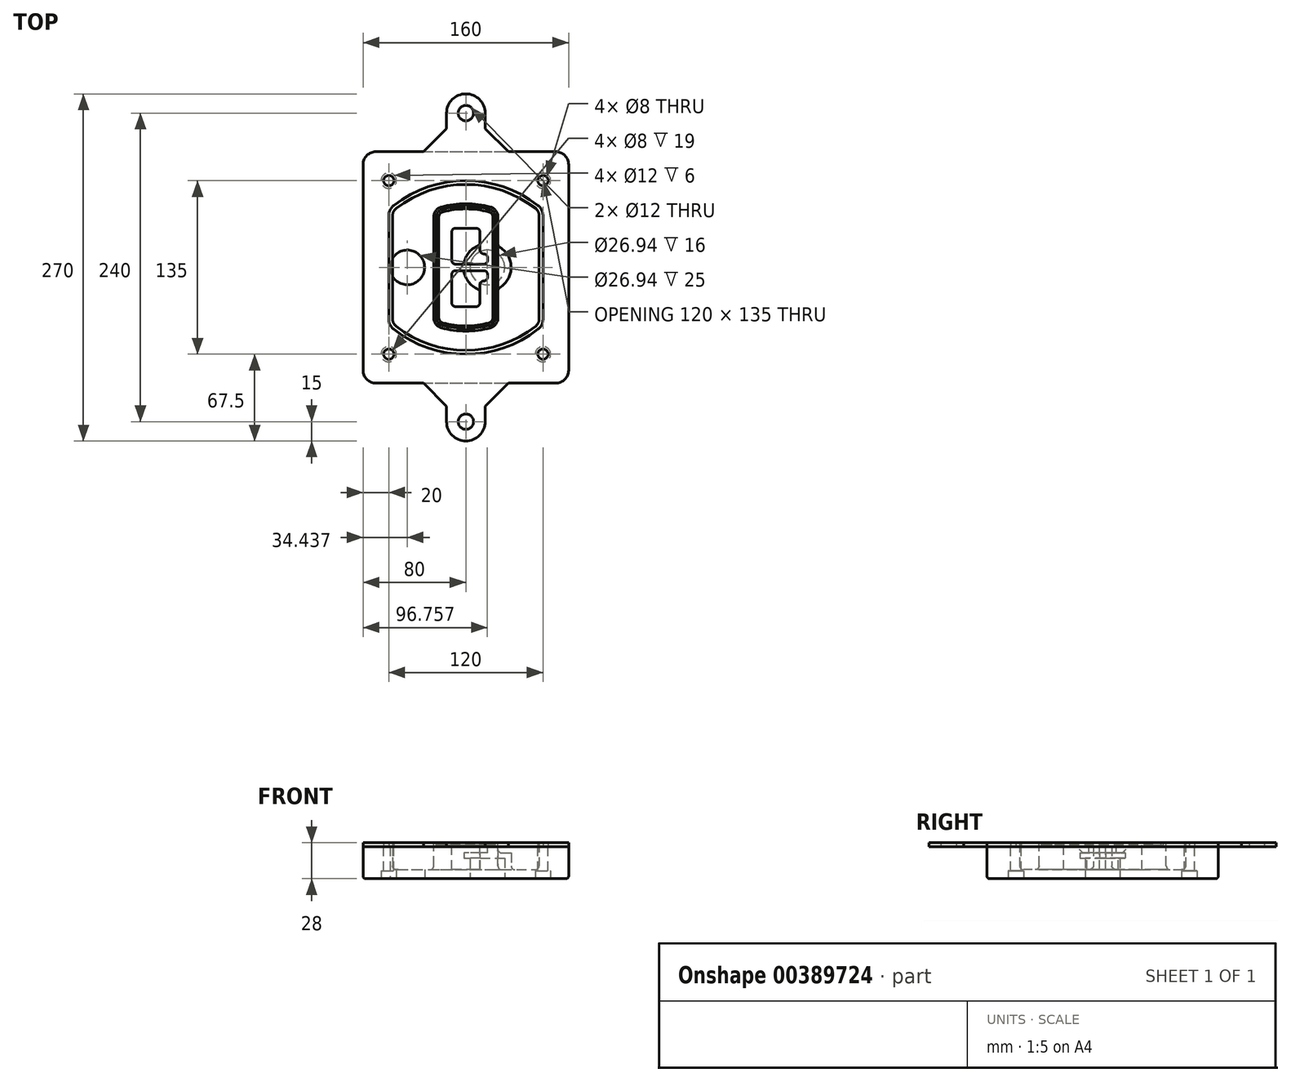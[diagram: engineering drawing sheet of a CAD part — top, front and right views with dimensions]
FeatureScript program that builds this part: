
annotation { "Feature Type Name" : "Feature", "Feature Type Description" : "" }
export const myFeature = defineFeature(function(context is Context, id is Id, definition is map)
    precondition{}
    {
        {
            var Q0;
            Q0=qCreatedBy(makeId("Top.planeOp"),FACE);
            var sketch = newSketch(context, id + "F0", { "sketchPlane" : qUnion([Q0])});
            skPoint(sketch, "E0.rect.middle", {"position": v(0, 0) * mm});
            skLineSegment(sketch, "E1.bottom", {"start": v(-70, -90) * mm, "end": v(70, -90) * mm});
            skLineSegment(sketch, "E1.top", {"start": v(-70, 90) * mm, "end": v(70, 90) * mm});
            skLineSegment(sketch, "E1.left", {"start": v(-80, -80) * mm, "end": v(-80, 80) * mm});
            skLineSegment(sketch, "E1.right", {"start": v(80, -80) * mm, "end": v(80, 80) * mm});
            skLineSegment(sketch, "E2", {"start": v(-80, 90) * mm, "end": v(80, -90) * mm, "construction": true});
            skLineSegment(sketch, "E3", {"start": v(80, 90) * mm, "end": v(-80, -90) * mm, "construction": true});
            skCircle(sketch, "E4", {"center": v(-60, 67.5) * mm, "radius": 4 * mm});
            skCircle(sketch, "E5", {"center": v(60, 67.5) * mm, "radius": 4 * mm});
            skCircle(sketch, "E6", {"center": v(60, -67.5) * mm, "radius": 4 * mm});
            skCircle(sketch, "E7", {"center": v(-60, -67.5) * mm, "radius": 4 * mm});
            skLineSegment(sketch, "E8", {"start": v(-60, 67.5) * mm, "end": v(60, 67.5) * mm, "construction": true});
            skLineSegment(sketch, "E9", {"start": v(60, 67.5) * mm, "end": v(60, -67.5) * mm, "construction": true});
            skLineSegment(sketch, "E10", {"start": v(60, -67.5) * mm, "end": v(-60, -67.5) * mm, "construction": true});
            skLineSegment(sketch, "E11", {"start": v(-60, -67.5) * mm, "end": v(-60, 67.5) * mm, "construction": true});
            skLineSegment(sketch, "E12", {"start": v(-60, 40.3) * mm, "end": v(-60, -40.3) * mm});
            skLineSegment(sketch, "E13", {"start": v(60, 40.3) * mm, "end": v(60, -40.3) * mm});
            skArc(sketch, "E14", {"start": v(56.15, 48.18) * mm, "mid": v(0, 67.5) * mm, "end": v(-56.15, 48.18) * mm});
            skArc(sketch, "E15", {"start": v(-56.15, -48.18) * mm, "mid": v(0, -67.5) * mm, "end": v(56.15, -48.18) * mm});
            skLineSegment(sketch, "E16", {"start": v(-60, 0) * mm, "end": v(60, 0) * mm, "construction": true});
            skPoint(sketch, "E17.visualSharp", {"position": v(-60, -45) * mm});
            skArc(sketch, "E17.filletArc", {"start": v(-60, -40.3) * mm, "mid": v(-58.99, -44.68) * mm, "end": v(-56.15, -48.18) * mm});
            skPoint(sketch, "E18.visualSharp", {"position": v(-60, 45) * mm});
            skArc(sketch, "E18.filletArc", {"start": v(-56.15, 48.18) * mm, "mid": v(-58.99, 44.68) * mm, "end": v(-60, 40.3) * mm});
            skPoint(sketch, "E19.visualSharp", {"position": v(60, 45) * mm});
            skArc(sketch, "E19.filletArc", {"start": v(60, 40.3) * mm, "mid": v(58.99, 44.68) * mm, "end": v(56.15, 48.18) * mm});
            skPoint(sketch, "E20.visualSharp", {"position": v(60, -45) * mm});
            skArc(sketch, "E20.filletArc", {"start": v(56.15, -48.18) * mm, "mid": v(58.99, -44.68) * mm, "end": v(60, -40.3) * mm});
            skPoint(sketch, "E21.visualSharp", {"position": v(-80, 90) * mm});
            skArc(sketch, "E21.filletArc", {"start": v(-70, 90) * mm, "mid": v(-77.07, 87.07) * mm, "end": v(-80, 80) * mm});
            skPoint(sketch, "E22.visualSharp", {"position": v(80, 90) * mm});
            skArc(sketch, "E22.filletArc", {"start": v(80, 80) * mm, "mid": v(77.07, 87.07) * mm, "end": v(70, 90) * mm});
            skPoint(sketch, "E23.visualSharp", {"position": v(80, -90) * mm});
            skArc(sketch, "E23.filletArc", {"start": v(70, -90) * mm, "mid": v(77.07, -87.07) * mm, "end": v(80, -80) * mm});
            skPoint(sketch, "E24.visualSharp", {"position": v(-80, -90) * mm});
            skArc(sketch, "E24.filletArc", {"start": v(-80, -80) * mm, "mid": v(-77.07, -87.07) * mm, "end": v(-70, -90) * mm});
            skArc(sketch, "E25.0", {"start": v(57, 40.3) * mm, "mid": v(56.3, 43.36) * mm, "end": v(54.3, 45.81) * mm});
            skLineSegment(sketch, "E25.1", {"start": v(57, 40.3) * mm, "end": v(57, -40.3) * mm});
            skArc(sketch, "E25.2", {"start": v(54.3, -45.81) * mm, "mid": v(56.3, -43.36) * mm, "end": v(57, -40.3) * mm});
            skArc(sketch, "E25.3", {"start": v(-54.3, -45.81) * mm, "mid": v(0, -64.5) * mm, "end": v(54.3, -45.81) * mm});
            skArc(sketch, "E25.4", {"start": v(-57, -40.3) * mm, "mid": v(-56.3, -43.36) * mm, "end": v(-54.3, -45.81) * mm});
            skArc(sketch, "E25.5", {"start": v(54.3, 45.81) * mm, "mid": v(0, 64.5) * mm, "end": v(-54.3, 45.81) * mm});
            skLineSegment(sketch, "E25.6", {"start": v(-57, 40.3) * mm, "end": v(-57, -40.3) * mm});
            skArc(sketch, "E25.7", {"start": v(-54.3, 45.81) * mm, "mid": v(-56.3, 43.36) * mm, "end": v(-57, 40.3) * mm});
            skArc(sketch, "E26.0", {"start": v(-58.62, 51.33) * mm, "mid": v(-62.58, 46.43) * mm, "end": v(-64, 40.3) * mm});
            skArc(sketch, "E26.1", {"start": v(58.62, 51.33) * mm, "mid": v(0, 71.5) * mm, "end": v(-58.62, 51.33) * mm});
            skArc(sketch, "E26.2", {"start": v(64, 40.3) * mm, "mid": v(62.58, 46.43) * mm, "end": v(58.62, 51.33) * mm});
            skLineSegment(sketch, "E26.3", {"start": v(64, 40.3) * mm, "end": v(64, -40.3) * mm});
            skArc(sketch, "E26.4", {"start": v(58.62, -51.33) * mm, "mid": v(62.58, -46.43) * mm, "end": v(64, -40.3) * mm});
            skLineSegment(sketch, "E26.5", {"start": v(-64, 40.3) * mm, "end": v(-64, -40.3) * mm});
            skArc(sketch, "E26.6", {"start": v(-58.62, -51.33) * mm, "mid": v(0, -71.5) * mm, "end": v(58.62, -51.33) * mm});
            skArc(sketch, "E26.7", {"start": v(-64, -40.3) * mm, "mid": v(-62.58, -46.43) * mm, "end": v(-58.62, -51.33) * mm});
            skSolve(sketch);
        }
        {
            var Q0;
            Q0=makeQuery(id+"F0.imprint","IMPRINT",FACE,{"disambiguationData":[TD([[makeQuery(id+"F0.imprint","IMPRINT",EDGE,{"derivedFrom":sQuery(id+"F0.wireOp",EDGE,"E1.bottom")}),1.0]])]});
            var Q1;
            Q1=makeQuery(id+"F0.imprint","IMPRINT",FACE,{"disambiguationData":[TD([[makeQuery(id+"F0.imprint","IMPRINT",EDGE,{"derivedFrom":sQuery(id+"F0.wireOp",EDGE,"E12")}),1.0]])]});
            var Q2;
            Q2=makeQuery(id+"F0.imprint","IMPRINT",FACE,{"disambiguationData":[TD([[makeQuery(id+"F0.imprint","IMPRINT",EDGE,{"derivedFrom":sQuery(id+"F0.wireOp",EDGE,"E25.0")}),1.0]])]});
            var Q3;
            Q3=makeQuery(id+"F0.imprint","IMPRINT",FACE,{"disambiguationData":[TD([[makeQuery(id+"F0.imprint","IMPRINT",EDGE,{"derivedFrom":sQuery(id+"F0.wireOp",EDGE,"E12")}),-1.0]])]});
            extrude(context, id + "F1", {"entities" : qUnion([Q0, Q1, Q2, Q3]), "oppositeDirection" : true, "depth" : 25 * mm});
        }
        {
            var Q0;
            Q0=makeQuery(id+"F0.imprint","IMPRINT",FACE,{"disambiguationData":[TD([[makeQuery(id+"F0.imprint","IMPRINT",EDGE,{"derivedFrom":sQuery(id+"F0.wireOp",EDGE,"E12")}),1.0]])]});
            extrude(context, id + "F2", {"entities" : qUnion([Q0]), "operationType" : NewBodyOperationType.ADD, "depth" : 3 * mm});
        }
        {
            var Q0;
            Q0=makeQuery(id+"F0.imprint","IMPRINT",FACE,{"disambiguationData":[TD([[makeQuery(id+"F0.imprint","IMPRINT",EDGE,{"derivedFrom":sQuery(id+"F0.wireOp",EDGE,"E25.0")}),1.0]])]});
            extrude(context, id + "F3", {"entities" : qUnion([Q0]), "operationType" : NewBodyOperationType.REMOVE, "oppositeDirection" : true, "depth" : 18 * mm});
        }
        {
            var Q0;
            Q0=makeQuery(id+"F2.opExtrude","CAP_FACE",FACE,{"disambiguationData":[OSD([sQuery(id+"F0.wireOp",EDGE,"E12"),sQuery(id+"F0.wireOp",EDGE,"E13"),sQuery(id+"F0.wireOp",EDGE,"E14"),sQuery(id+"F0.wireOp",EDGE,"E15"),sQuery(id+"F0.wireOp",EDGE,"E17.filletArc"),sQuery(id+"F0.wireOp",EDGE,"E18.filletArc"),sQuery(id+"F0.wireOp",EDGE,"E19.filletArc"),sQuery(id+"F0.wireOp",EDGE,"E20.filletArc"),sQuery(id+"F0.wireOp",EDGE,"E25.0"),sQuery(id+"F0.wireOp",EDGE,"E25.1"),sQuery(id+"F0.wireOp",EDGE,"E25.2"),sQuery(id+"F0.wireOp",EDGE,"E25.3"),sQuery(id+"F0.wireOp",EDGE,"E25.4"),sQuery(id+"F0.wireOp",EDGE,"E25.5"),sQuery(id+"F0.wireOp",EDGE,"E25.6"),sQuery(id+"F0.wireOp",EDGE,"E25.7")])],"isStart":false});
            var sketch = newSketch(context, id + "F4", { "sketchPlane" : qUnion([Q0])});
            skArc(sketch, "E27.0", {"start": v(-19.08, -46.97) * mm, "mid": v(0, -49.5) * mm, "end": v(19.08, -46.97) * mm});
            skArc(sketch, "E28.0", {"start": v(19.08, 46.97) * mm, "mid": v(0, 49.5) * mm, "end": v(-19.08, 46.97) * mm});
            skLineSegment(sketch, "E29", {"start": v(-25, 39.25) * mm, "end": v(-25, -39.25) * mm});
            skLineSegment(sketch, "E30", {"start": v(25, 39.25) * mm, "end": v(25, -39.25) * mm});
            skLineSegment(sketch, "E31", {"start": v(-25, 45.1) * mm, "end": v(25, 45.1) * mm, "construction": true});
            skLineSegment(sketch, "E32", {"start": v(-25, -45.1) * mm, "end": v(25, -45.1) * mm, "construction": true});
            skPoint(sketch, "E33.visualSharp", {"position": v(-25, 45.1) * mm});
            skArc(sketch, "E33.filletArc", {"start": v(-19.08, 46.97) * mm, "mid": v(-23.35, 44.11) * mm, "end": v(-25, 39.25) * mm});
            skPoint(sketch, "E34.visualSharp", {"position": v(25, 45.1) * mm});
            skArc(sketch, "E34.filletArc", {"start": v(25, 39.25) * mm, "mid": v(23.35, 44.11) * mm, "end": v(19.08, 46.97) * mm});
            skPoint(sketch, "E35.visualSharp", {"position": v(25, -45.1) * mm});
            skArc(sketch, "E35.filletArc", {"start": v(19.08, -46.97) * mm, "mid": v(23.35, -44.11) * mm, "end": v(25, -39.25) * mm});
            skPoint(sketch, "E36.visualSharp", {"position": v(-25, -45.1) * mm});
            skArc(sketch, "E36.filletArc", {"start": v(-25, -39.25) * mm, "mid": v(-23.35, -44.11) * mm, "end": v(-19.08, -46.97) * mm});
            skArc(sketch, "E37.0", {"start": v(54.3, 45.81) * mm, "mid": v(0, 64.5) * mm, "end": v(-54.3, 45.81) * mm});
            skArc(sketch, "E37.1", {"start": v(-54.3, 45.81) * mm, "mid": v(-56.3, 43.36) * mm, "end": v(-57, 40.3) * mm});
            skLineSegment(sketch, "E37.2", {"start": v(-57, 40.3) * mm, "end": v(-57, -40.3) * mm});
            skArc(sketch, "E37.3", {"start": v(-57, -40.3) * mm, "mid": v(-56.3, -43.36) * mm, "end": v(-54.3, -45.81) * mm});
            skArc(sketch, "E37.4", {"start": v(-54.3, -45.81) * mm, "mid": v(0, -64.5) * mm, "end": v(54.3, -45.81) * mm});
            skArc(sketch, "E37.5", {"start": v(54.3, -45.81) * mm, "mid": v(56.3, -43.36) * mm, "end": v(57, -40.3) * mm});
            skLineSegment(sketch, "E37.6", {"start": v(57, 40.3) * mm, "end": v(57, -40.3) * mm});
            skArc(sketch, "E37.7", {"start": v(57, 40.3) * mm, "mid": v(56.3, 43.36) * mm, "end": v(54.3, 45.81) * mm});
            skLineSegment(sketch, "E38.0", {"start": v(23, 39.25) * mm, "end": v(23, -39.25) * mm});
            skArc(sketch, "E38.1", {"start": v(18.56, -45.04) * mm, "mid": v(21.76, -42.9) * mm, "end": v(23, -39.25) * mm});
            skArc(sketch, "E38.2", {"start": v(-18.56, -45.04) * mm, "mid": v(0, -47.5) * mm, "end": v(18.56, -45.04) * mm});
            skArc(sketch, "E38.3", {"start": v(-23, -39.25) * mm, "mid": v(-21.76, -42.9) * mm, "end": v(-18.56, -45.04) * mm});
            skLineSegment(sketch, "E38.4", {"start": v(-23, 39.25) * mm, "end": v(-23, -39.25) * mm});
            skArc(sketch, "E38.5", {"start": v(23, 39.25) * mm, "mid": v(21.76, 42.9) * mm, "end": v(18.56, 45.04) * mm});
            skArc(sketch, "E38.6", {"start": v(-18.56, 45.04) * mm, "mid": v(-21.76, 42.9) * mm, "end": v(-23, 39.25) * mm});
            skArc(sketch, "E38.7", {"start": v(18.56, 45.04) * mm, "mid": v(0, 47.5) * mm, "end": v(-18.56, 45.04) * mm});
            skArc(sketch, "E39.0", {"start": v(21, 39.25) * mm, "mid": v(20.18, 41.68) * mm, "end": v(18.04, 43.1) * mm});
            skLineSegment(sketch, "E39.1", {"start": v(21, 39.25) * mm, "end": v(21, -39.25) * mm});
            skArc(sketch, "E39.2", {"start": v(18.04, -43.1) * mm, "mid": v(20.18, -41.68) * mm, "end": v(21, -39.25) * mm});
            skArc(sketch, "E39.3", {"start": v(-18.04, -43.1) * mm, "mid": v(0, -45.5) * mm, "end": v(18.04, -43.1) * mm});
            skArc(sketch, "E39.4", {"start": v(-21, -39.25) * mm, "mid": v(-20.18, -41.68) * mm, "end": v(-18.04, -43.1) * mm});
            skArc(sketch, "E39.5", {"start": v(18.04, 43.1) * mm, "mid": v(0, 45.5) * mm, "end": v(-18.04, 43.1) * mm});
            skLineSegment(sketch, "E39.6", {"start": v(-21, 39.25) * mm, "end": v(-21, -39.25) * mm});
            skArc(sketch, "E39.7", {"start": v(-18.04, 43.1) * mm, "mid": v(-20.18, 41.68) * mm, "end": v(-21, 39.25) * mm});
            skLineSegment(sketch, "E40", {"start": v(-25, 0) * mm, "end": v(25, 0) * mm, "construction": true});
            skLineSegment(sketch, "E41", {"start": v(-11, 5.5) * mm, "end": v(-11, 27.5) * mm});
            skLineSegment(sketch, "E42", {"start": v(-8, 30.5) * mm, "end": v(8, 30.5) * mm});
            skLineSegment(sketch, "E43", {"start": v(11, 27.5) * mm, "end": v(11, 13.5) * mm});
            skLineSegment(sketch, "E44", {"start": v(14, 10.5) * mm, "end": v(14, 10.5) * mm});
            skLineSegment(sketch, "E45", {"start": v(17, 7.5) * mm, "end": v(17, 5.5) * mm});
            skLineSegment(sketch, "E46", {"start": v(14, 2.5) * mm, "end": v(-8, 2.5) * mm});
            skPoint(sketch, "E47.visualSharp", {"position": v(-11, 30.5) * mm});
            skArc(sketch, "E47.filletArc", {"start": v(-8, 30.5) * mm, "mid": v(-10.12, 29.62) * mm, "end": v(-11, 27.5) * mm});
            skPoint(sketch, "E48.visualSharp", {"position": v(11, 30.5) * mm});
            skArc(sketch, "E48.filletArc", {"start": v(11, 27.5) * mm, "mid": v(10.12, 29.62) * mm, "end": v(8, 30.5) * mm});
            skPoint(sketch, "E49.visualSharp", {"position": v(11, 10.5) * mm});
            skArc(sketch, "E49.filletArc", {"start": v(11, 13.5) * mm, "mid": v(11.88, 11.38) * mm, "end": v(14, 10.5) * mm});
            skPoint(sketch, "E50.visualSharp", {"position": v(17, 10.5) * mm});
            skArc(sketch, "E50.filletArc", {"start": v(17, 7.5) * mm, "mid": v(16.12, 9.62) * mm, "end": v(14, 10.5) * mm});
            skPoint(sketch, "E51.visualSharp", {"position": v(17, 2.5) * mm});
            skArc(sketch, "E51.filletArc", {"start": v(14, 2.5) * mm, "mid": v(16.12, 3.38) * mm, "end": v(17, 5.5) * mm});
            skPoint(sketch, "E52.visualSharp", {"position": v(-11, 2.5) * mm});
            skArc(sketch, "E52.filletArc", {"start": v(-11, 5.5) * mm, "mid": v(-10.12, 3.38) * mm, "end": v(-8, 2.5) * mm});
            skLineSegment(sketch, "E53.0.MirrorCS", {"start": v(14, -2.5) * mm, "end": v(-8, -2.5) * mm});
            skArc(sketch, "E54.0.MirrorCS", {"start": v(-11, -5.5) * mm, "mid": v(-10.12, -3.38) * mm, "end": v(-8, -2.5) * mm});
            skLineSegment(sketch, "E55.0.MirrorCS", {"start": v(-11, -5.5) * mm, "end": v(-11, -27.5) * mm});
            skArc(sketch, "E56.0.MirrorCS", {"start": v(-8, -30.5) * mm, "mid": v(-10.12, -29.62) * mm, "end": v(-11, -27.5) * mm});
            skLineSegment(sketch, "E57.0.MirrorCS", {"start": v(-8, -30.5) * mm, "end": v(8, -30.5) * mm});
            skArc(sketch, "E58.0.MirrorCS", {"start": v(11, -27.5) * mm, "mid": v(10.12, -29.62) * mm, "end": v(8, -30.5) * mm});
            skLineSegment(sketch, "E59.0.MirrorCS", {"start": v(11, -27.5) * mm, "end": v(11, -13.5) * mm});
            skArc(sketch, "E60.0.MirrorCS", {"start": v(11, -13.5) * mm, "mid": v(11.88, -11.38) * mm, "end": v(14, -10.5) * mm});
            skArc(sketch, "E61.0.MirrorCS", {"start": v(17, -7.5) * mm, "mid": v(16.12, -9.62) * mm, "end": v(14, -10.5) * mm});
            skLineSegment(sketch, "E62.0.MirrorCS", {"start": v(17, -7.5) * mm, "end": v(17, -5.5) * mm});
            skArc(sketch, "E63.0.MirrorCS", {"start": v(14, -2.5) * mm, "mid": v(16.12, -3.38) * mm, "end": v(17, -5.5) * mm});
            skSolve(sketch);
        }
        {
            var Q0;
            Q0=makeQuery(id+"F4.imprint","IMPRINT",FACE,{"disambiguationData":[TD([[makeQuery(id+"F4.imprint","IMPRINT",EDGE,{"derivedFrom":sQuery(id+"F4.wireOp",EDGE,"E27.0")}),1.0]])]});
            var Q1;
            Q1=makeQuery(id+"F4.imprint","IMPRINT",FACE,{"disambiguationData":[TD([[makeQuery(id+"F4.imprint","IMPRINT",EDGE,{"derivedFrom":sQuery(id+"F4.wireOp",EDGE,"E38.0")}),-1.0]])]});
            var Q2;
            Q2=makeQuery(id+"F4.imprint","IMPRINT",FACE,{"disambiguationData":[TD([[makeQuery(id+"F4.imprint","IMPRINT",EDGE,{"derivedFrom":sQuery(id+"F4.wireOp",EDGE,"E39.0")}),1.0]])]});
            extrude(context, id + "F5", {"entities" : qUnion([Q0, Q1, Q2]), "operationType" : NewBodyOperationType.ADD, "endBound" : BoundingType.UP_TO_NEXT, "oppositeDirection" : true, "depth" : 25 * mm});
        }
        {
            var Q0;
            Q0=makeQuery(id+"F4.imprint","IMPRINT",FACE,{"disambiguationData":[TD([[makeQuery(id+"F4.imprint","IMPRINT",EDGE,{"derivedFrom":sQuery(id+"F4.wireOp",EDGE,"E38.0")}),-1.0]])]});
            extrude(context, id + "F6", {"entities" : qUnion([Q0]), "operationType" : NewBodyOperationType.REMOVE, "oppositeDirection" : true, "depth" : 2 * mm});
        }
        {
            var Q0;
            Q0=makeQuery(id+"F1.opExtrude","CAP_FACE",FACE,{"disambiguationData":[OSD([sQuery(id+"F0.wireOp",EDGE,"E1.bottom"),sQuery(id+"F0.wireOp",EDGE,"E1.top"),sQuery(id+"F0.wireOp",EDGE,"E1.left"),sQuery(id+"F0.wireOp",EDGE,"E1.right"),sQuery(id+"F0.wireOp",EDGE,"E4"),sQuery(id+"F0.wireOp",EDGE,"E5"),sQuery(id+"F0.wireOp",EDGE,"E6"),sQuery(id+"F0.wireOp",EDGE,"E7"),sQuery(id+"F0.wireOp",EDGE,"E21.filletArc"),sQuery(id+"F0.wireOp",EDGE,"E22.filletArc"),sQuery(id+"F0.wireOp",EDGE,"E23.filletArc"),sQuery(id+"F0.wireOp",EDGE,"E24.filletArc")])],"isStart":false});
            var sketch = newSketch(context, id + "F7", { "sketchPlane" : qUnion([Q0])});
            skCircle(sketch, "E64", {"center": v(16.76, 0) * mm, "radius": 13.47 * mm});
            skCircle(sketch, "E65", {"center": v(-45.56, 0) * mm, "radius": 13.47 * mm});
            skLineSegment(sketch, "E66", {"start": v(80, 0) * mm, "end": v(-80, 0) * mm});
            skCircle(sketch, "E67", {"center": v(16.76, 0) * mm, "radius": 18.47 * mm});
            skCircle(sketch, "E68", {"center": v(60, -67.5) * mm, "radius": 6 * mm});
            skCircle(sketch, "E69", {"center": v(-60, -67.5) * mm, "radius": 6 * mm});
            skCircle(sketch, "E70", {"center": v(-60, 67.5) * mm, "radius": 6 * mm});
            skCircle(sketch, "E71", {"center": v(60, 67.5) * mm, "radius": 6 * mm});
            skSolve(sketch);
        }
        {
            var Q0;
            {var subQ1=sQuery(id+"F7.wireOp",EDGE,"E66");var subQ4=sQuery(id+"F7.wireOp",EDGE,"E64");var subQ6=makeQuery(id+"F7.imprint","INTERSECT",VERTEX,{"disambiguationData":[OD(0.0)],"derivedFrom":[subQ4,subQ1]});Q0=makeQuery(id+"F7.imprint","IMPRINT",FACE,{"disambiguationData":[TD([[makeQuery(id+"F7.imprint","IMPRINT",EDGE,{"disambiguationData":[TD([[subQ6,-1.0]])],"derivedFrom":subQ4}),-1.0]])]});}
            var Q1;
            {var subQ0=sQuery(id+"F7.wireOp",EDGE,"E66");var subQ1=sQuery(id+"F7.wireOp",EDGE,"E64");var subQ3=makeQuery(id+"F7.imprint","INTERSECT",VERTEX,{"disambiguationData":[OD(0.0)],"derivedFrom":[subQ1,subQ0]});Q1=makeQuery(id+"F7.imprint","IMPRINT",FACE,{"disambiguationData":[TD([[makeQuery(id+"F7.imprint","IMPRINT",EDGE,{"disambiguationData":[TD([[subQ3,-1.0]])],"derivedFrom":subQ1}),1.0]])]});}
            var Q2;
            {var subQ0=sQuery(id+"F7.wireOp",EDGE,"E66");var subQ1=sQuery(id+"F7.wireOp",EDGE,"E64");var subQ3=makeQuery(id+"F7.imprint","INTERSECT",VERTEX,{"disambiguationData":[OD(0.0)],"derivedFrom":[subQ1,subQ0]});Q2=makeQuery(id+"F7.imprint","IMPRINT",FACE,{"disambiguationData":[TD([[makeQuery(id+"F7.imprint","IMPRINT",EDGE,{"disambiguationData":[TD([[subQ3,1.0]])],"derivedFrom":subQ1}),1.0]])]});}
            var Q3;
            {var subQ1=sQuery(id+"F7.wireOp",EDGE,"E66");var subQ4=sQuery(id+"F7.wireOp",EDGE,"E64");var subQ6=makeQuery(id+"F7.imprint","INTERSECT",VERTEX,{"disambiguationData":[OD(0.0)],"derivedFrom":[subQ4,subQ1]});Q3=makeQuery(id+"F7.imprint","IMPRINT",FACE,{"disambiguationData":[TD([[makeQuery(id+"F7.imprint","IMPRINT",EDGE,{"disambiguationData":[TD([[subQ6,1.0]])],"derivedFrom":subQ4}),-1.0]])]});}
            extrude(context, id + "F8", {"entities" : qUnion([Q0, Q1, Q2, Q3]), "operationType" : NewBodyOperationType.ADD, "oppositeDirection" : true, "depth" : 20 * mm});
        }
        {
            var Q0;
            {var subQ0=sQuery(id+"F7.wireOp",EDGE,"E66");var subQ1=sQuery(id+"F7.wireOp",EDGE,"E64");var subQ3=makeQuery(id+"F7.imprint","INTERSECT",VERTEX,{"disambiguationData":[OD(0.0)],"derivedFrom":[subQ1,subQ0]});Q0=makeQuery(id+"F7.imprint","IMPRINT",FACE,{"disambiguationData":[TD([[makeQuery(id+"F7.imprint","IMPRINT",EDGE,{"disambiguationData":[TD([[subQ3,-1.0]])],"derivedFrom":subQ1}),1.0]])]});}
            var Q1;
            {var subQ0=sQuery(id+"F7.wireOp",EDGE,"E66");var subQ1=sQuery(id+"F7.wireOp",EDGE,"E64");var subQ3=makeQuery(id+"F7.imprint","INTERSECT",VERTEX,{"disambiguationData":[OD(0.0)],"derivedFrom":[subQ1,subQ0]});Q1=makeQuery(id+"F7.imprint","IMPRINT",FACE,{"disambiguationData":[TD([[makeQuery(id+"F7.imprint","IMPRINT",EDGE,{"disambiguationData":[TD([[subQ3,1.0]])],"derivedFrom":subQ1}),1.0]])]});}
            extrude(context, id + "F9", {"entities" : qUnion([Q0, Q1]), "operationType" : NewBodyOperationType.REMOVE, "oppositeDirection" : true, "depth" : 16 * mm});
        }
        {
            var Q0;
            {var subQ0=sQuery(id+"F7.wireOp",EDGE,"E66");var subQ1=sQuery(id+"F7.wireOp",EDGE,"E65");var subQ3=makeQuery(id+"F7.imprint","INTERSECT",VERTEX,{"disambiguationData":[OD(0.0)],"derivedFrom":[subQ1,subQ0]});Q0=makeQuery(id+"F7.imprint","IMPRINT",FACE,{"disambiguationData":[TD([[makeQuery(id+"F7.imprint","IMPRINT",EDGE,{"disambiguationData":[TD([[subQ3,-1.0]])],"derivedFrom":subQ1}),1.0]])]});}
            var Q1;
            {var subQ0=sQuery(id+"F7.wireOp",EDGE,"E66");var subQ1=sQuery(id+"F7.wireOp",EDGE,"E65");var subQ3=makeQuery(id+"F7.imprint","INTERSECT",VERTEX,{"disambiguationData":[OD(0.0)],"derivedFrom":[subQ1,subQ0]});Q1=makeQuery(id+"F7.imprint","IMPRINT",FACE,{"disambiguationData":[TD([[makeQuery(id+"F7.imprint","IMPRINT",EDGE,{"disambiguationData":[TD([[subQ3,1.0]])],"derivedFrom":subQ1}),1.0]])]});}
            extrude(context, id + "F10", {"entities" : qUnion([Q0, Q1]), "operationType" : NewBodyOperationType.REMOVE, "oppositeDirection" : true, "depth" : 25 * mm});
        }
        {
            var Q0;
            Q0=makeQuery(id+"F7.imprint","IMPRINT",FACE,{"disambiguationData":[TD([[makeQuery(id+"F7.imprint","IMPRINT",EDGE,{"derivedFrom":sQuery(id+"F7.wireOp",EDGE,"E68")}),1.0]])]});
            var Q1;
            Q1=makeQuery(id+"F7.imprint","IMPRINT",FACE,{"disambiguationData":[TD([[makeQuery(id+"F7.imprint","IMPRINT",EDGE,{"derivedFrom":makeQuery(id+"F1.opExtrude","CAP_EDGE",EDGE,{"disambiguationData":[OSD([sQuery(id+"F0.wireOp",EDGE,"E5")])],"isStart":false})}),-1.0]])]});
            var Q2;
            Q2=makeQuery(id+"F7.imprint","IMPRINT",FACE,{"disambiguationData":[TD([[makeQuery(id+"F7.imprint","IMPRINT",EDGE,{"derivedFrom":sQuery(id+"F7.wireOp",EDGE,"E69")}),1.0]])]});
            var Q3;
            Q3=makeQuery(id+"F7.imprint","IMPRINT",FACE,{"disambiguationData":[TD([[makeQuery(id+"F7.imprint","IMPRINT",EDGE,{"derivedFrom":makeQuery(id+"F1.opExtrude","CAP_EDGE",EDGE,{"disambiguationData":[OSD([sQuery(id+"F0.wireOp",EDGE,"E4")])],"isStart":false})}),-1.0]])]});
            var Q4;
            Q4=makeQuery(id+"F7.imprint","IMPRINT",FACE,{"disambiguationData":[TD([[makeQuery(id+"F7.imprint","IMPRINT",EDGE,{"derivedFrom":sQuery(id+"F7.wireOp",EDGE,"E70")}),1.0]])]});
            var Q5;
            Q5=makeQuery(id+"F7.imprint","IMPRINT",FACE,{"disambiguationData":[TD([[makeQuery(id+"F7.imprint","IMPRINT",EDGE,{"derivedFrom":makeQuery(id+"F1.opExtrude","CAP_EDGE",EDGE,{"disambiguationData":[OSD([sQuery(id+"F0.wireOp",EDGE,"E7")])],"isStart":false})}),-1.0]])]});
            var Q6;
            Q6=makeQuery(id+"F7.imprint","IMPRINT",FACE,{"disambiguationData":[TD([[makeQuery(id+"F7.imprint","IMPRINT",EDGE,{"derivedFrom":sQuery(id+"F7.wireOp",EDGE,"E71")}),1.0]])]});
            var Q7;
            Q7=makeQuery(id+"F7.imprint","IMPRINT",FACE,{"disambiguationData":[TD([[makeQuery(id+"F7.imprint","IMPRINT",EDGE,{"derivedFrom":makeQuery(id+"F1.opExtrude","CAP_EDGE",EDGE,{"disambiguationData":[OSD([sQuery(id+"F0.wireOp",EDGE,"E6")])],"isStart":false})}),-1.0]])]});
            extrude(context, id + "F11", {"entities" : qUnion([Q0, Q1, Q2, Q3, Q4, Q5, Q6, Q7]), "operationType" : NewBodyOperationType.REMOVE, "oppositeDirection" : true, "depth" : 6 * mm});
        }
        {
            var Q0;
            Q0=makeQuery(id+"F9.boolean.opBoolean","COPY",FACE,{"derivedFrom":makeQuery(id+"F9.opExtrude","CAP_FACE",FACE,{"disambiguationData":[OSD([sQuery(id+"F7.wireOp",EDGE,"E64")])],"isStart":false})});
            var sketch = newSketch(context, id + "F12", { "sketchPlane" : qUnion([Q0])});
            skArc(sketch, "E72.0", {"start": v(11, 17.55) * mm, "mid": v(2.57, 11.82) * mm, "end": v(-1.54, 2.5) * mm});
            skArc(sketch, "E72.1", {"start": v(-1.54, -2.5) * mm, "mid": v(2.57, -11.82) * mm, "end": v(11, -17.55) * mm});
            skLineSegment(sketch, "E73", {"start": v(-1.54, -2.5) * mm, "end": v(14, -2.5) * mm});
            skLineSegment(sketch, "E74.0", {"start": v(14, 2.5) * mm, "end": v(-1.54, 2.5) * mm});
            skArc(sketch, "E74.1", {"start": v(14, 2.5) * mm, "mid": v(16.12, 3.38) * mm, "end": v(17, 5.5) * mm});
            skLineSegment(sketch, "E74.2", {"start": v(17, 7.5) * mm, "end": v(17, 5.5) * mm});
            skArc(sketch, "E74.3", {"start": v(17, 7.5) * mm, "mid": v(16.12, 9.62) * mm, "end": v(14, 10.5) * mm});
            skArc(sketch, "E74.4", {"start": v(11, 13.5) * mm, "mid": v(11.88, 11.38) * mm, "end": v(14, 10.5) * mm});
            skLineSegment(sketch, "E74.5", {"start": v(11, 17.55) * mm, "end": v(11, 13.5) * mm});
            skLineSegment(sketch, "E74.7", {"start": v(14, -2.5) * mm, "end": v(-1.54, -2.5) * mm});
            skArc(sketch, "E74.8", {"start": v(14, -2.5) * mm, "mid": v(16.12, -3.38) * mm, "end": v(17, -5.5) * mm});
            skLineSegment(sketch, "E74.9", {"start": v(17, -7.5) * mm, "end": v(17, -5.5) * mm});
            skArc(sketch, "E74.10", {"start": v(17, -7.5) * mm, "mid": v(16.12, -9.62) * mm, "end": v(14, -10.5) * mm});
            skArc(sketch, "E74.11", {"start": v(11, -13.5) * mm, "mid": v(11.88, -11.38) * mm, "end": v(14, -10.5) * mm});
            skLineSegment(sketch, "E74.12", {"start": v(11, -17.55) * mm, "end": v(11, -13.5) * mm});
            skPoint(sketch, "E75.orphan", {"position": v(11, -27.5) * mm});
            skPoint(sketch, "E76.orphan", {"position": v(-8, -2.5) * mm});
            skPoint(sketch, "E77.orphan", {"position": v(-8, 2.5) * mm});
            skPoint(sketch, "E78.orphan", {"position": v(11, 27.5) * mm});
            skSolve(sketch);
        }
        {
            var Q0;
            {var subQ7=sQuery(id+"F12.wireOp",EDGE,"E72.0");var subQ14=sQuery(id+"F12.wireOp",EDGE,"E72.1");var subQ16=sQuery(id+"F12.wireOp",EDGE,"E74.1");var subQ18=sQuery(id+"F12.wireOp",EDGE,"E74.8");Q0=qUnion([makeQuery(id+"F12.imprint","IMPRINT",FACE,{"disambiguationData":[TD([[makeQuery(id+"F12.imprint","IMPRINT",EDGE,{"derivedFrom":subQ7}),1.0]])]}),makeQuery(id+"F12.imprint","IMPRINT",FACE,{"disambiguationData":[TD([[makeQuery(id+"F12.imprint","IMPRINT",EDGE,{"derivedFrom":subQ14}),1.0]])]}),makeQuery(id+"F12.imprint","IMPRINT",FACE,{"disambiguationData":[TD([[makeQuery(id+"F12.imprint","IMPRINT",EDGE,{"derivedFrom":subQ16}),1.0]])]}),makeQuery(id+"F12.imprint","IMPRINT",FACE,{"disambiguationData":[TD([[makeQuery(id+"F12.imprint","IMPRINT",EDGE,{"derivedFrom":subQ18}),-1.0]])]})]);}
            var Q1;
            Q1=makeQuery(id+"F5.boolean.opBoolean","SPLIT",FACE,{"disambiguationData":[TD([makeQuery(id+"F5.opExtrude","SWEPT_FACE",FACE,{"disambiguationData":[OSD([sQuery(id+"F4.wireOp",EDGE,"E41")])]})])],"derivedFrom":makeQuery(id+"F3.boolean.opBoolean","COPY",FACE,{"derivedFrom":makeQuery(id+"F3.opExtrude","CAP_FACE",FACE,{"disambiguationData":[OSD([sQuery(id+"F0.wireOp",EDGE,"E25.0"),sQuery(id+"F0.wireOp",EDGE,"E25.1"),sQuery(id+"F0.wireOp",EDGE,"E25.2"),sQuery(id+"F0.wireOp",EDGE,"E25.3"),sQuery(id+"F0.wireOp",EDGE,"E25.4"),sQuery(id+"F0.wireOp",EDGE,"E25.5"),sQuery(id+"F0.wireOp",EDGE,"E25.6"),sQuery(id+"F0.wireOp",EDGE,"E25.7")])],"isStart":false})})});
            extrude(context, id + "F13", {"entities" : qUnion([Q0]), "operationType" : NewBodyOperationType.REMOVE, "endBound" : BoundingType.UP_TO_SURFACE, "endBoundEntityFace" : qUnion([Q1]), "depth" : 25 * mm});
        }
        {
            var Q0;
            Q0=makeQuery(id+"F3.boolean.opBoolean","COPY",EDGE,{"derivedFrom":makeQuery(id+"F3.opExtrude","CAP_EDGE",EDGE,{"disambiguationData":[OSD([sQuery(id+"F0.wireOp",EDGE,"E25.6")])],"isStart":false})});
            var Q1;
            Q1=makeQuery(id+"F8.boolean.opBoolean","INTERSECT",EDGE,{"derivedFrom":[makeQuery(id+"F5.opExtrude","SWEPT_FACE",FACE,{"disambiguationData":[OSD([sQuery(id+"F4.wireOp",EDGE,"E30")])]}),makeQuery(id+"F8.opExtrude","CAP_FACE",FACE,{"disambiguationData":[OSD([sQuery(id+"F7.wireOp",EDGE,"E67")])],"isStart":false})]});
            var Q2;
            Q2=makeQuery(id+"F8.boolean.opBoolean","INTERSECT",EDGE,{"disambiguationData":[OD(1.0)],"derivedFrom":[makeQuery(id+"F5.opExtrude","SWEPT_FACE",FACE,{"disambiguationData":[OSD([sQuery(id+"F4.wireOp",EDGE,"E30")])]}),makeQuery(id+"F8.opExtrude","SWEPT_FACE",FACE,{"disambiguationData":[OSD([sQuery(id+"F7.wireOp",EDGE,"E67")])]})]});
            var Q3;
            {var subQ0=sQuery(id+"F4.wireOp",EDGE,"E30");Q3=makeQuery(id+"F8.boolean.opBoolean","SPLIT",EDGE,{"disambiguationData":[TD([makeQuery(id+"F5.opExtrude","SWEPT_FACE",FACE,{"disambiguationData":[OSD([sQuery(id+"F4.wireOp",EDGE,"E35.filletArc")])]})])],"derivedFrom":makeQuery(id+"F5.opExtrude","CAP_EDGE",EDGE,{"disambiguationData":[OSD([subQ0])],"isStart":false})});}
            var Q4;
            {var subQ0=sQuery(id+"F0.wireOp",EDGE,"E25.7");var subQ1=sQuery(id+"F0.wireOp",EDGE,"E25.1");var subQ2=sQuery(id+"F0.wireOp",EDGE,"E25.6");var subQ3=sQuery(id+"F0.wireOp",EDGE,"E25.5");var subQ4=sQuery(id+"F0.wireOp",EDGE,"E25.4");var subQ5=sQuery(id+"F0.wireOp",EDGE,"E25.0");var subQ6=sQuery(id+"F0.wireOp",EDGE,"E25.2");var subQ7=sQuery(id+"F0.wireOp",EDGE,"E25.3");Q4=makeQuery(id+"F8.boolean.opBoolean","INTERSECT",EDGE,{"derivedFrom":[makeQuery(id+"F5.boolean.opBoolean","SPLIT",FACE,{"disambiguationData":[TD([makeQuery(id+"F2.opExtrude","SWEPT_FACE",FACE,{"disambiguationData":[OSD([subQ5])]})])],"derivedFrom":makeQuery(id+"F3.boolean.opBoolean","COPY",FACE,{"derivedFrom":makeQuery(id+"F3.opExtrude","CAP_FACE",FACE,{"disambiguationData":[OSD([subQ5,subQ1,subQ6,subQ7,subQ4,subQ3,subQ2,subQ0])],"isStart":false})})}),makeQuery(id+"F8.opExtrude","SWEPT_FACE",FACE,{"disambiguationData":[OSD([sQuery(id+"F7.wireOp",EDGE,"E67")])]})]});}
            var Q5;
            Q5=makeQuery(id+"F8.boolean.opBoolean","INTERSECT",EDGE,{"disambiguationData":[OD(0.0)],"derivedFrom":[makeQuery(id+"F5.opExtrude","SWEPT_FACE",FACE,{"disambiguationData":[OSD([sQuery(id+"F4.wireOp",EDGE,"E30")])]}),makeQuery(id+"F8.opExtrude","SWEPT_FACE",FACE,{"disambiguationData":[OSD([sQuery(id+"F7.wireOp",EDGE,"E67")])]})]});
            fillet(context, id + "F14", {"entities" : qUnion([Q0, Q1, Q2, Q3, Q4, Q5]), "radius" : 3 * mm, "tangentPropagation" : true, "allowEdgeOverflow" : false});
        }
        {
            var Q0;
            Q0=makeQuery(id+"F1.opExtrude","CAP_EDGE",EDGE,{"disambiguationData":[OSD([sQuery(id+"F0.wireOp",EDGE,"E1.bottom")])],"isStart":false});
            fillet(context, id + "F15", {"entities" : qUnion([Q0]), "radius" : 2 * mm, "tangentPropagation" : true, "allowEdgeOverflow" : false});
        }
        {
            var Q0;
            {var subQ0=sQuery(id+"F0.wireOp",EDGE,"E21.filletArc");var subQ1=sQuery(id+"F0.wireOp",EDGE,"E7");var subQ2=sQuery(id+"F0.wireOp",EDGE,"E6");var subQ3=sQuery(id+"F0.wireOp",EDGE,"E5");var subQ4=sQuery(id+"F0.wireOp",EDGE,"E4");var subQ5=sQuery(id+"F0.wireOp",EDGE,"E22.filletArc");var subQ6=sQuery(id+"F0.wireOp",EDGE,"E1.bottom");var subQ7=sQuery(id+"F0.wireOp",EDGE,"E1.right");var subQ8=sQuery(id+"F0.wireOp",EDGE,"E1.top");var subQ9=sQuery(id+"F0.wireOp",EDGE,"E1.left");var subQ10=sQuery(id+"F0.wireOp",EDGE,"E23.filletArc");var subQ11=sQuery(id+"F0.wireOp",EDGE,"E24.filletArc");Q0=makeQuery(id+"F2.boolean.opBoolean","SPLIT",FACE,{"disambiguationData":[TD([makeQuery(id+"F1.opExtrude","SWEPT_FACE",FACE,{"disambiguationData":[OSD([subQ6])]})])],"derivedFrom":makeQuery(id+"F1.opExtrude","CAP_FACE",FACE,{"disambiguationData":[OSD([subQ6,subQ8,subQ9,subQ7,subQ4,subQ3,subQ2,subQ1,subQ0,subQ5,subQ10,subQ11])],"isStart":true})});}
            var sketch = newSketch(context, id + "F16", { "sketchPlane" : qUnion([Q0])});
            skSolve(sketch);
        }
        {
            var Q0;
            Q0=makeQuery(id+"F16.imprint","IMPRINT",FACE,{"disambiguationData":[TD([[makeQuery(id+"F16.imprint","IMPRINT",EDGE,{"derivedFrom":makeQuery(id+"F1.opExtrude","CAP_EDGE",EDGE,{"disambiguationData":[OSD([sQuery(id+"F0.wireOp",EDGE,"E1.bottom")])],"isStart":true})}),1.0]])]});
            var sketch = newSketch(context, id + "F17", { "sketchPlane" : qUnion([Q0])});
            skLineSegment(sketch, "E79.0", {"start": v(80, -80) * mm, "end": v(80, 80) * mm});
            skArc(sketch, "E79.1", {"start": v(80, 80) * mm, "mid": v(77.07, 87.07) * mm, "end": v(70, 90) * mm});
            skLineSegment(sketch, "E79.2", {"start": v(70, 90) * mm, "end": v(-70, 90) * mm});
            skArc(sketch, "E79.3", {"start": v(-70, 90) * mm, "mid": v(-77.07, 87.07) * mm, "end": v(-80, 80) * mm});
            skLineSegment(sketch, "E79.4", {"start": v(-80, -80) * mm, "end": v(-80, 80) * mm});
            skArc(sketch, "E79.5", {"start": v(-80, -80) * mm, "mid": v(-77.07, -87.07) * mm, "end": v(-70, -90) * mm});
            skLineSegment(sketch, "E79.6", {"start": v(-70, -90) * mm, "end": v(70, -90) * mm});
            skArc(sketch, "E79.7", {"start": v(70, -90) * mm, "mid": v(77.07, -87.07) * mm, "end": v(80, -80) * mm});
            skCircle(sketch, "E79.8", {"center": v(60, -67.5) * mm, "radius": 4 * mm});
            skCircle(sketch, "E79.9", {"center": v(60, 67.5) * mm, "radius": 4 * mm});
            skCircle(sketch, "E79.10", {"center": v(-60, 67.5) * mm, "radius": 4 * mm});
            skCircle(sketch, "E79.11", {"center": v(-60, -67.5) * mm, "radius": 4 * mm});
            skArc(sketch, "E79.12", {"start": v(-56.15, -48.18) * mm, "mid": v(0, -67.5) * mm, "end": v(56.15, -48.18) * mm});
            skArc(sketch, "E79.13", {"start": v(-60, -40.3) * mm, "mid": v(-58.99, -44.68) * mm, "end": v(-56.15, -48.18) * mm});
            skLineSegment(sketch, "E79.14", {"start": v(-60, 40.3) * mm, "end": v(-60, -40.3) * mm});
            skArc(sketch, "E79.15", {"start": v(56.15, 48.18) * mm, "mid": v(0, 67.5) * mm, "end": v(-56.15, 48.18) * mm});
            skArc(sketch, "E79.16", {"start": v(-56.15, 48.18) * mm, "mid": v(-58.99, 44.68) * mm, "end": v(-60, 40.3) * mm});
            skArc(sketch, "E79.17", {"start": v(60, 40.3) * mm, "mid": v(58.99, 44.68) * mm, "end": v(56.15, 48.18) * mm});
            skLineSegment(sketch, "E79.18", {"start": v(60, 40.3) * mm, "end": v(60, -40.3) * mm});
            skArc(sketch, "E79.19", {"start": v(56.15, -48.18) * mm, "mid": v(58.99, -44.68) * mm, "end": v(60, -40.3) * mm});
            skLineSegment(sketch, "E80", {"start": v(-33, 90) * mm, "end": v(-15, 108) * mm});
            skLineSegment(sketch, "E81", {"start": v(-15, 108) * mm, "end": v(-15, 120) * mm});
            skLineSegment(sketch, "E82", {"start": v(33, 90) * mm, "end": v(15, 108) * mm});
            skLineSegment(sketch, "E83", {"start": v(15, 108) * mm, "end": v(15, 120) * mm});
            skArc(sketch, "E84", {"start": v(15, 120) * mm, "mid": v(0, 135) * mm, "end": v(-15, 120) * mm});
            skCircle(sketch, "E85", {"center": v(0, 120) * mm, "radius": 6 * mm});
            skLineSegment(sketch, "E86", {"start": v(-80, 0) * mm, "end": v(80, 0) * mm, "construction": true});
            skLineSegment(sketch, "E87.MirrorCS", {"start": v(-33, -90) * mm, "end": v(-15, -108) * mm});
            skLineSegment(sketch, "E88.MirrorCS", {"start": v(33, -90) * mm, "end": v(15, -108) * mm});
            skLineSegment(sketch, "E89.MirrorCS", {"start": v(15, -108) * mm, "end": v(15, -120) * mm});
            skCircle(sketch, "E90.MirrorC", {"center": v(0, -120) * mm, "radius": 6 * mm});
            skLineSegment(sketch, "E91.MirrorCS", {"start": v(-15, -108) * mm, "end": v(-15, -120) * mm});
            skArc(sketch, "E92.MirrorCS", {"start": v(15, -120) * mm, "mid": v(0, -135) * mm, "end": v(-15, -120) * mm});
            skSolve(sketch);
        }
        {
            var Q0;
            Q0=qSketchRegion(id+"F17",true);
            var Q1;
            Q1=makeQuery(id+"F2.opExtrude","CAP_FACE",FACE,{"disambiguationData":[OSD([sQuery(id+"F0.wireOp",EDGE,"E12"),sQuery(id+"F0.wireOp",EDGE,"E13"),sQuery(id+"F0.wireOp",EDGE,"E14"),sQuery(id+"F0.wireOp",EDGE,"E15"),sQuery(id+"F0.wireOp",EDGE,"E17.filletArc"),sQuery(id+"F0.wireOp",EDGE,"E18.filletArc"),sQuery(id+"F0.wireOp",EDGE,"E19.filletArc"),sQuery(id+"F0.wireOp",EDGE,"E20.filletArc"),sQuery(id+"F0.wireOp",EDGE,"E25.0"),sQuery(id+"F0.wireOp",EDGE,"E25.1"),sQuery(id+"F0.wireOp",EDGE,"E25.2"),sQuery(id+"F0.wireOp",EDGE,"E25.3"),sQuery(id+"F0.wireOp",EDGE,"E25.4"),sQuery(id+"F0.wireOp",EDGE,"E25.5"),sQuery(id+"F0.wireOp",EDGE,"E25.6"),sQuery(id+"F0.wireOp",EDGE,"E25.7")])],"isStart":false});
            extrude(context, id + "F18", {"entities" : qUnion([Q0]), "endBound" : BoundingType.UP_TO_SURFACE, "endBoundEntityFace" : qUnion([Q1]), "depth" : 25 * mm});
        }
    });
